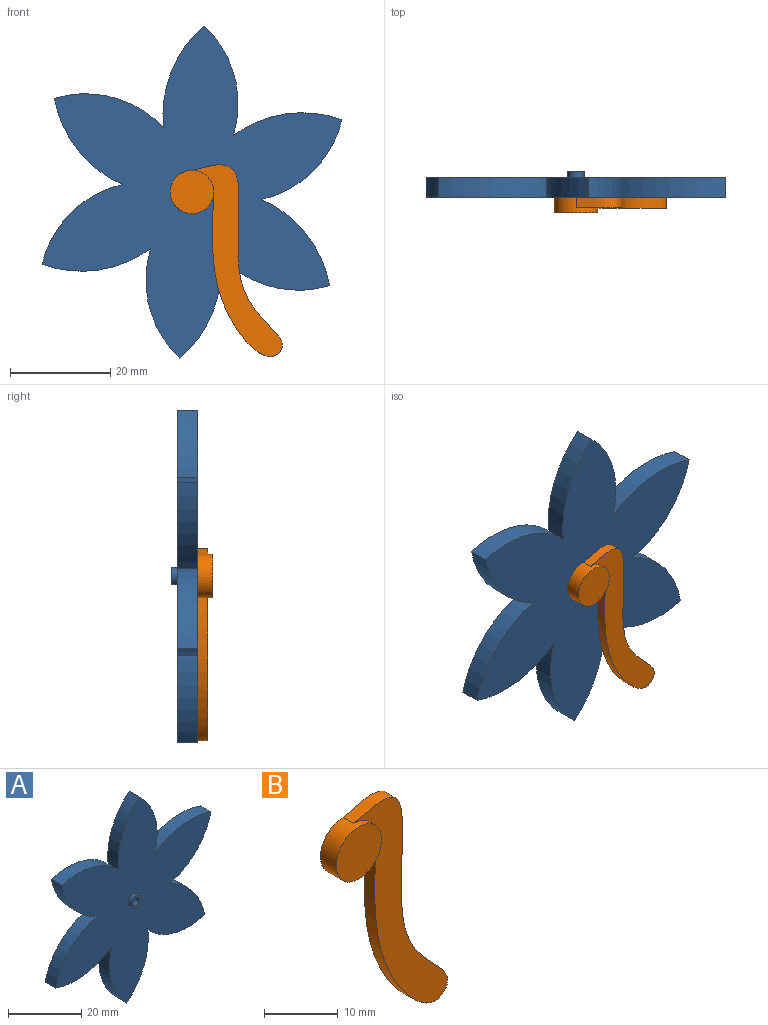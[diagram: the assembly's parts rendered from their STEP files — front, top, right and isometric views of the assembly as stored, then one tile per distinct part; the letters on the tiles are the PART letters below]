
ASSEMBLY  parts=2 mates=1
PART A: 19 faces, bbox 60x6.5x66.4 mm
  f0: cylinder r=23.3mm len=17.22mm, axis (0,-1,0), area 92.8mm2, adj f1,f11,f12,f13
  f1: cylinder r=21.4mm len=16.03mm, axis (0,-1,0), area 96.9mm2, adj f0,f2,f12,f13
  f2: cylinder r=23.3mm len=21.7mm, axis (0,-1,0), area 92.8mm2, adj f1,f3,f12,f13
  f3: cylinder r=21.4mm len=21.87mm, axis (0,-1,0), area 96.9mm2, adj f2,f4,f12,f13
  f4: cylinder r=23.3mm len=20.36mm, axis (0,-1,0), area 92.8mm2, adj f3,f5,f12,f13
  f5: cylinder r=21.4mm len=21.85mm, axis (0,-1,0), area 96.9mm2, adj f4,f6,f12,f13
  f6: cylinder r=23.3mm len=17.22mm, axis (0,-1,0), area 92.8mm2, adj f5,f7,f12,f13
  f7: cylinder r=21.4mm len=16.03mm, axis (0,-1,0), area 96.9mm2, adj f6,f8,f12,f13
  f8: cylinder r=23.3mm len=21.7mm, axis (0,-1,0), area 92.8mm2, adj f7,f9,f12,f13
  f9: cylinder r=21.4mm len=21.87mm, axis (0,-1,0), area 96.9mm2, adj f8,f10,f12,f13
  f10: cylinder r=23.3mm len=20.36mm, axis (0,-1,0), area 92.8mm2, adj f9,f11,f12,f13
  f11: cylinder r=21.4mm len=21.85mm, axis (0,-1,0), area 96.9mm2, adj f0,f10,f12,f13
  f12: plane 66.39x59.96mm, normal (0,1,0), area 1932.9mm2, adj f0,f1,f2,f3,f4,f5,f6,f7
  f13: plane 66.39x59.96mm, normal (0,-1,0), area 1928.6mm2, adj f0,f1,f2,f3,f4,f5,f6,f7
  f14: cylinder r=1.27mm len=6.48mm, axis (0,-1,0), area 51.7mm2, adj f16,f18
  f15: cylinder r=2.02mm len=4.05mm, axis (0,1,0), area 14.5mm2, adj f13,f16
  f16: plane 4.05x4.05mm, normal (0,-1,0), area 7.8mm2, adj f14,f15
  f17: cylinder r=1.65mm len=3.31mm, axis (0,-1,0), area 13.2mm2, adj f12,f18
  f18: plane 3.31x3.31mm, normal (0,1,0), area 3.5mm2, adj f14,f17
PART B: 6 faces, bbox 23.3x3.1x40.2 mm
  f0: extruded ~38.27x18.05mm, area 177mm2, adj f1,f2,f4
  f1: plane 40.24x18.97mm, normal (0,-1,0), area 209.7mm2, adj f0,f3,f4
  f2: plane 40.23x23.31mm, normal (0,1,0), area 269.2mm2, adj f0,f4
  f3: extruded ~1.02x0.46mm, area 0.5mm2, adj f1,f4,f5
  f4: cylinder r=4.35mm len=8.7mm, axis (0,1,0), area 68mm2, adj f0,f1,f2,f3,f5
  f5: plane 8.7x8.7mm, normal (0,-1,0), area 59.4mm2, adj f3,f4
PLACE A t=(33.93,-6.69,3.45)mm
PLACE B t=(33.93,-6.69,3.45)mm
MATE revolute B.f4 <-> A.f15  axis (0,1,0) through (33.93,-6.69,3.45)mm
